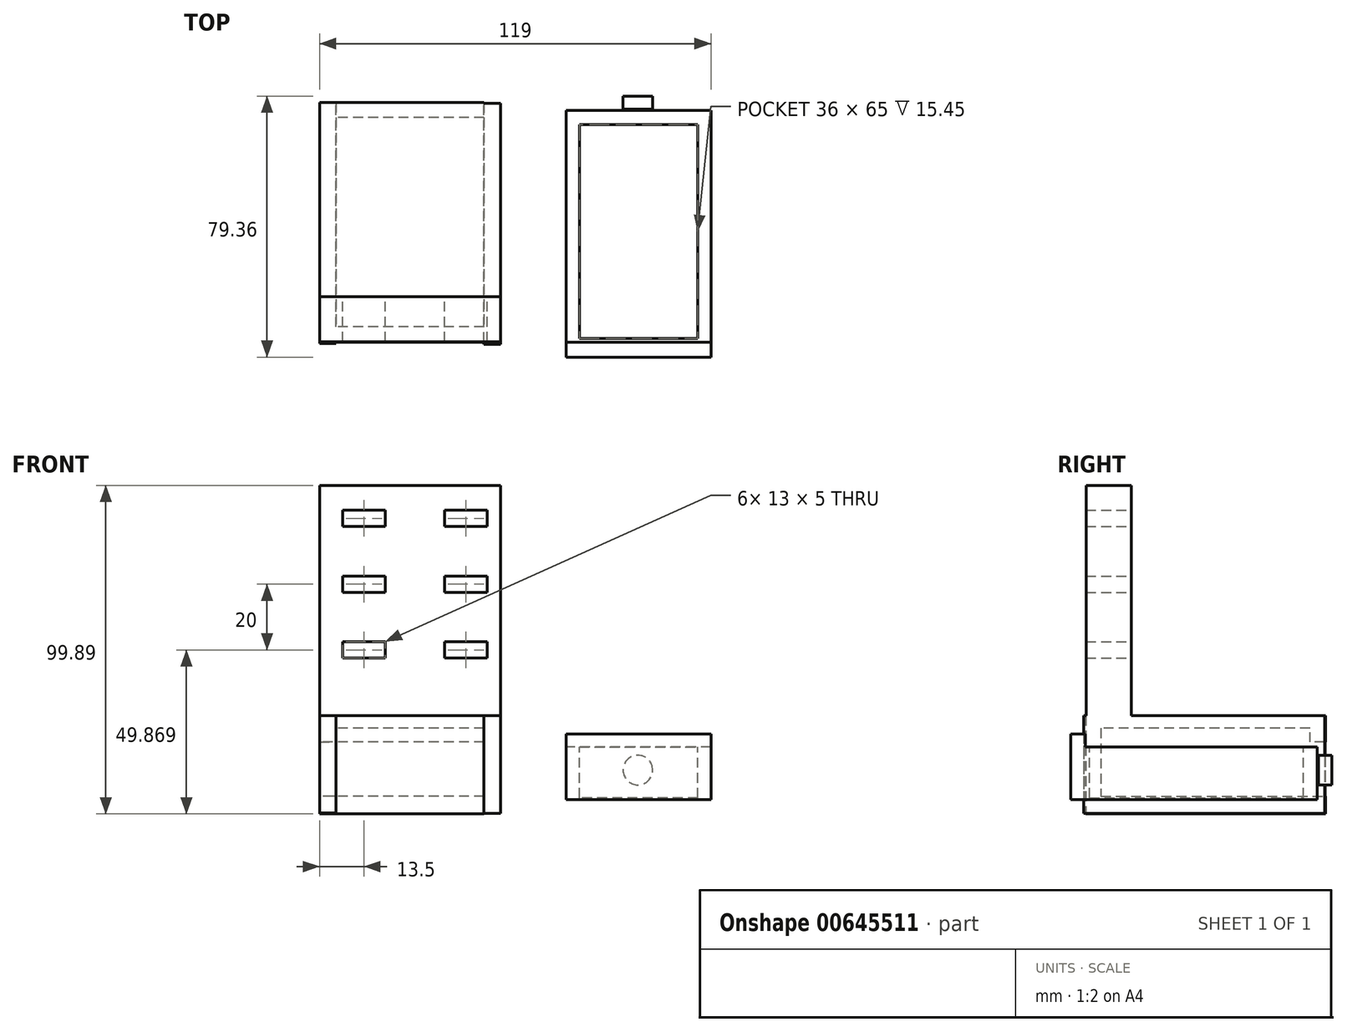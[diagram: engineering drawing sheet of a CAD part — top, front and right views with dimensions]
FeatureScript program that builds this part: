
annotation { "Feature Type Name" : "Feature", "Feature Type Description" : "" }
export const myFeature = defineFeature(function(context is Context, id is Id, definition is map)
    precondition{}
    {
        {
            var Q0;
            Q0=qCreatedBy(makeId("Right.planeOp"),FACE);
            var sketch = newSketch(context, id + "F0", { "sketchPlane" : qUnion([Q0])});
            skLineSegment(sketch, "E0.bottom", {"start": v(-47.39, 0) * mm, "end": v(25.52, 0) * mm});
            skLineSegment(sketch, "E0.top", {"start": v(-47.39, -29.9) * mm, "end": v(25.52, -29.9) * mm});
            skLineSegment(sketch, "E0.left", {"start": v(-47.39, 0) * mm, "end": v(-47.39, -29.9) * mm});
            skLineSegment(sketch, "E0.right", {"start": v(25.52, 0) * mm, "end": v(25.52, -8.02) * mm});
            skLineSegment(sketch, "E1", {"start": v(25.52, -29.9) * mm, "end": v(25.52, -29.9) * mm});
            skLineSegment(sketch, "E2", {"start": v(25.52, -8.02) * mm, "end": v(20.85, -8.02) * mm});
            skLineSegment(sketch, "E3", {"start": v(20.85, -8.02) * mm, "end": v(20.85, -3.86) * mm});
            skLineSegment(sketch, "E4", {"start": v(20.85, -3.86) * mm, "end": v(-42.77, -3.86) * mm});
            skLineSegment(sketch, "E5", {"start": v(-42.77, -3.86) * mm, "end": v(-42.77, -24.55) * mm});
            skLineSegment(sketch, "E6", {"start": v(-42.77, -24.55) * mm, "end": v(25.52, -24.55) * mm});
            skLineSegment(sketch, "E7", {"start": v(25.52, -24.55) * mm, "end": v(25.52, -29.9) * mm});
            skSolve(sketch);
        }
        {
            var Q0;
            Q0 = qSketchRegion(id + "F0", true);
            extrude(context, id + "F1", {"entities" : qUnion([Q0]), "depth" : 30 * mm, "offsetDistance" : 25 * mm, "hasSecondDirection" : true, "secondDirectionOppositeDirection" : true, "secondDirectionDepth" : 20 * mm});
        }
        {
            var Q0;
            Q0=qCreatedBy(makeId("Right.planeOp"),FACE);
            cPlane(context, id + "F2", {"entities" : qUnion([Q0]), "cplaneType" : CPlaneType.OFFSET, "offset" : 30 * mm, "width" : 150 * mm, "height" : 150 * mm});
        }
        {
            var Q0;
            Q0=qCreatedBy(id+"F2.planeOp",FACE);
            var sketch = newSketch(context, id + "F3", { "sketchPlane" : qUnion([Q0])});
            skLineSegment(sketch, "E8.bottom", {"start": v(-48.01, 0) * mm, "end": v(25.24, 0) * mm});
            skLineSegment(sketch, "E8.top", {"start": v(-48.01, -29.75) * mm, "end": v(25.24, -29.75) * mm});
            skLineSegment(sketch, "E8.left", {"start": v(-48.01, 0) * mm, "end": v(-48.01, -29.75) * mm});
            skLineSegment(sketch, "E8.right", {"start": v(25.24, 0) * mm, "end": v(25.24, -29.75) * mm});
            skSolve(sketch);
        }
        {
            var Q0;
            Q0 = qSketchRegion(id + "F3", true);
            extrude(context, id + "F4", {"entities" : qUnion([Q0]), "operationType" : NewBodyOperationType.ADD, "depth" : 5 * mm, "offsetDistance" : 25 * mm});
        }
        {
            var Q0;
            Q0=qCreatedBy(makeId("Right.planeOp"),FACE);
            var sketch = newSketch(context, id + "F5", { "sketchPlane" : qUnion([Q0])});
            skLineSegment(sketch, "E9.bottom", {"start": v(-47.26, 0) * mm, "end": v(-33.58, 0) * mm});
            skLineSegment(sketch, "E9.top", {"start": v(-47.26, 70) * mm, "end": v(-33.58, 70) * mm});
            skLineSegment(sketch, "E9.left", {"start": v(-47.26, 0) * mm, "end": v(-47.26, 70) * mm});
            skLineSegment(sketch, "E9.right", {"start": v(-33.58, 0) * mm, "end": v(-33.58, 70) * mm});
            skSolve(sketch);
        }
        {
            var Q0;
            Q0 = qSketchRegion(id + "F5", true);
            extrude(context, id + "F6", {"entities" : qUnion([Q0]), "operationType" : NewBodyOperationType.ADD, "depth" : 35 * mm, "offsetDistance" : 25 * mm, "hasSecondDirection" : true, "secondDirectionOppositeDirection" : true, "secondDirectionDepth" : 20 * mm});
        }
        {
            var Q0;
            Q0=qCreatedBy(makeId("Right.planeOp"),FACE);
            cPlane(context, id + "F7", {"entities" : qUnion([Q0]), "cplaneType" : CPlaneType.OFFSET, "offset" : 55 * mm, "width" : 150 * mm, "height" : 150 * mm});
        }
        {
            var Q0;
            Q0=qCreatedBy(id+"F7.planeOp",FACE);
            var sketch = newSketch(context, id + "F8", { "sketchPlane" : qUnion([Q0])});
            skLineSegment(sketch, "E10.top", {"start": v(23.04, -25.55) * mm, "end": v(-51.96, -25.55) * mm});
            skLineSegment(sketch, "E10.left", {"start": v(23.04, -9.55) * mm, "end": v(23.04, -25.55) * mm});
            skLineSegment(sketch, "E10.right", {"start": v(-51.96, -9.55) * mm, "end": v(-51.96, -25.55) * mm});
            skLineSegment(sketch, "E11", {"start": v(-51.96, -9.55) * mm, "end": v(-51.96, -5.55) * mm});
            skLineSegment(sketch, "E12", {"start": v(-51.96, -5.55) * mm, "end": v(-47.45, -5.55) * mm});
            skLineSegment(sketch, "E13", {"start": v(-47.45, -5.55) * mm, "end": v(-47.45, -9.55) * mm});
            skLineSegment(sketch, "E14", {"start": v(23.04, -9.55) * mm, "end": v(-47.45, -9.55) * mm});
            skPoint(sketch, "E15.end.orphan", {"position": v(42.24, -5.55) * mm});
            skPoint(sketch, "E16.end.orphan", {"position": v(36.47, -5.55) * mm});
            skSolve(sketch);
        }
        {
            var Q0;
            Q0 = qSketchRegion(id + "F8", true);
            extrude(context, id + "F9", {"entities" : qUnion([Q0]), "depth" : 44 * mm, "offsetDistance" : 25 * mm});
        }
        {
            var Q0;
            Q0=qCreatedBy(makeId("Top.planeOp"),FACE);
            var sketch = newSketch(context, id + "F10", { "sketchPlane" : qUnion([Q0])});
            skLineSegment(sketch, "E17.bottom", {"start": v(95, -46.22) * mm, "end": v(59, -46.22) * mm});
            skLineSegment(sketch, "E17.top", {"start": v(95, 18.78) * mm, "end": v(59, 18.78) * mm});
            skLineSegment(sketch, "E17.left", {"start": v(95, -46.22) * mm, "end": v(95, 18.78) * mm});
            skLineSegment(sketch, "E17.right", {"start": v(59, -46.22) * mm, "end": v(59, 18.78) * mm});
            skSolve(sketch);
        }
        {
            var Q0;
            Q0 = qSketchRegion(id + "F10", true);
            extrude(context, id + "F11", {"entities" : qUnion([Q0]), "operationType" : NewBodyOperationType.REMOVE, "oppositeDirection" : true, "depth" : 25 * mm, "offsetDistance" : 25 * mm});
        }
        {
            var Q0;
            Q0=qCreatedBy(makeId("Front.planeOp"),FACE);
            cPlane(context, id + "F12", {"entities" : qUnion([Q0]), "cplaneType" : CPlaneType.OFFSET, "offset" : 40.2 * mm, "oppositeDirection" : true, "width" : 150 * mm, "height" : 150 * mm});
        }
        {
            var Q0;
            Q0=qCreatedBy(id+"F12.planeOp",FACE);
            var sketch = newSketch(context, id + "F13", { "sketchPlane" : qUnion([Q0])});
            skCircle(sketch, "E18", {"center": v(69.58, -16.54) * mm, "radius": 4.5 * mm});
            skSolve(sketch);
        }
        {
            var Q0;
            Q0 = qSketchRegion(id + "F13", true);
            extrude(context, id + "F14", {"entities" : qUnion([Q0]), "operationType" : NewBodyOperationType.ADD, "oppositeDirection" : true, "depth" : 4 * mm, "offsetDistance" : 25 * mm});
        }
        {
            var Q0;
            Q0=makeQuery(id+"F14.opExtrude","SWEPT_BODY",BODY,{"disambiguationData":[OSD([sQuery(id+"F13.wireOp",EDGE,"E18")])]});
            var Q1;
            Q1=makeQuery(id+"F11.boolean.opBoolean","INTERSECT",EDGE,{"derivedFrom":[makeQuery(id+"F9.opExtrude","SWEPT_FACE",FACE,{"disambiguationData":[OSD([sQuery(id+"F8.wireOp",EDGE,"E10.left")])]}),makeQuery(id+"F11.opExtrude","SWEPT_FACE",FACE,{"disambiguationData":[OSD([sQuery(id+"F10.wireOp",EDGE,"E17.left")])]})]});
            transform(context, id + "F15", {"entities" : qUnion([Q0]), "transformType" : TransformType.TRANSLATION_3D, "dx" : 7.2 * mm, "dy" : -16.8 * mm, "dz" : 0 * mm, "makeCopy" : false});
        }
        {
            var Q0;
            Q0=qCreatedBy(makeId("Right.planeOp"),FACE);
            cPlane(context, id + "F16", {"entities" : qUnion([Q0]), "cplaneType" : CPlaneType.OFFSET, "offset" : 20 * mm, "oppositeDirection" : true, "width" : 150 * mm, "height" : 150 * mm});
        }
        {
            var Q0;
            Q0=qCreatedBy(id+"F16.planeOp",FACE);
            var sketch = newSketch(context, id + "F17", { "sketchPlane" : qUnion([Q0])});
            skLineSegment(sketch, "E19.bottom", {"start": v(-47.85, 0) * mm, "end": v(25.4, 0) * mm});
            skLineSegment(sketch, "E19.top", {"start": v(-47.85, -29.55) * mm, "end": v(25.4, -29.55) * mm});
            skLineSegment(sketch, "E19.left", {"start": v(-47.85, 0) * mm, "end": v(-47.85, -29.55) * mm});
            skLineSegment(sketch, "E19.right", {"start": v(25.4, 0) * mm, "end": v(25.4, -29.55) * mm});
            skSolve(sketch);
        }
        {
            var Q0;
            Q0 = qSketchRegion(id + "F17", true);
            extrude(context, id + "F18", {"entities" : qUnion([Q0]), "operationType" : NewBodyOperationType.ADD, "depth" : 5 * mm, "offsetDistance" : 25 * mm});
        }
        {
            var Q0;
            Q0=qCreatedBy(makeId("Front.planeOp"),FACE);
            var sketch = newSketch(context, id + "F19", { "sketchPlane" : qUnion([Q0])});
            skLineSegment(sketch, "E20.bottom", {"start": v(31, 62.48) * mm, "end": v(18, 62.48) * mm});
            skLineSegment(sketch, "E20.top", {"start": v(31, 57.48) * mm, "end": v(18, 57.48) * mm});
            skLineSegment(sketch, "E20.left", {"start": v(31, 62.48) * mm, "end": v(31, 57.48) * mm});
            skLineSegment(sketch, "E20.right", {"start": v(18, 62.48) * mm, "end": v(18, 57.48) * mm});
            skLineSegment(sketch, "E21.bottom", {"start": v(0, 62.48) * mm, "end": v(-13, 62.48) * mm});
            skLineSegment(sketch, "E21.top", {"start": v(0, 57.48) * mm, "end": v(-13, 57.48) * mm});
            skLineSegment(sketch, "E21.left", {"start": v(0, 62.48) * mm, "end": v(0, 57.48) * mm});
            skLineSegment(sketch, "E21.right", {"start": v(-13, 62.48) * mm, "end": v(-13, 57.48) * mm});
            skLineSegment(sketch, "E22.bottom", {"start": v(31, 42.48) * mm, "end": v(18, 42.48) * mm});
            skLineSegment(sketch, "E22.top", {"start": v(31, 37.48) * mm, "end": v(18, 37.48) * mm});
            skLineSegment(sketch, "E22.left", {"start": v(31, 42.48) * mm, "end": v(31, 37.48) * mm});
            skLineSegment(sketch, "E22.right", {"start": v(18, 42.48) * mm, "end": v(18, 37.48) * mm});
            skLineSegment(sketch, "E23.bottom", {"start": v(0, 42.48) * mm, "end": v(-13, 42.48) * mm});
            skLineSegment(sketch, "E23.top", {"start": v(0, 37.48) * mm, "end": v(-13, 37.48) * mm});
            skLineSegment(sketch, "E23.left", {"start": v(0, 42.48) * mm, "end": v(0, 37.48) * mm});
            skLineSegment(sketch, "E23.right", {"start": v(-13, 42.48) * mm, "end": v(-13, 37.48) * mm});
            skLineSegment(sketch, "E24.bottom", {"start": v(31, 22.48) * mm, "end": v(18, 22.48) * mm});
            skLineSegment(sketch, "E24.top", {"start": v(31, 17.48) * mm, "end": v(18, 17.48) * mm});
            skLineSegment(sketch, "E24.left", {"start": v(31, 22.48) * mm, "end": v(31, 17.48) * mm});
            skLineSegment(sketch, "E24.right", {"start": v(18, 22.48) * mm, "end": v(18, 17.48) * mm});
            skLineSegment(sketch, "E25.bottom", {"start": v(0, 22.48) * mm, "end": v(-13, 22.48) * mm});
            skLineSegment(sketch, "E25.top", {"start": v(0, 17.48) * mm, "end": v(-13, 17.48) * mm});
            skLineSegment(sketch, "E25.left", {"start": v(0, 22.48) * mm, "end": v(0, 17.48) * mm});
            skLineSegment(sketch, "E25.right", {"start": v(-13, 22.48) * mm, "end": v(-13, 17.48) * mm});
            skSolve(sketch);
        }
        {
            var Q0;
            Q0 = qSketchRegion(id + "F19", true);
            extrude(context, id + "F20", {"entities" : qUnion([Q0]), "operationType" : NewBodyOperationType.REMOVE, "depth" : 63 * mm, "offsetDistance" : 25 * mm});
        }
    });
